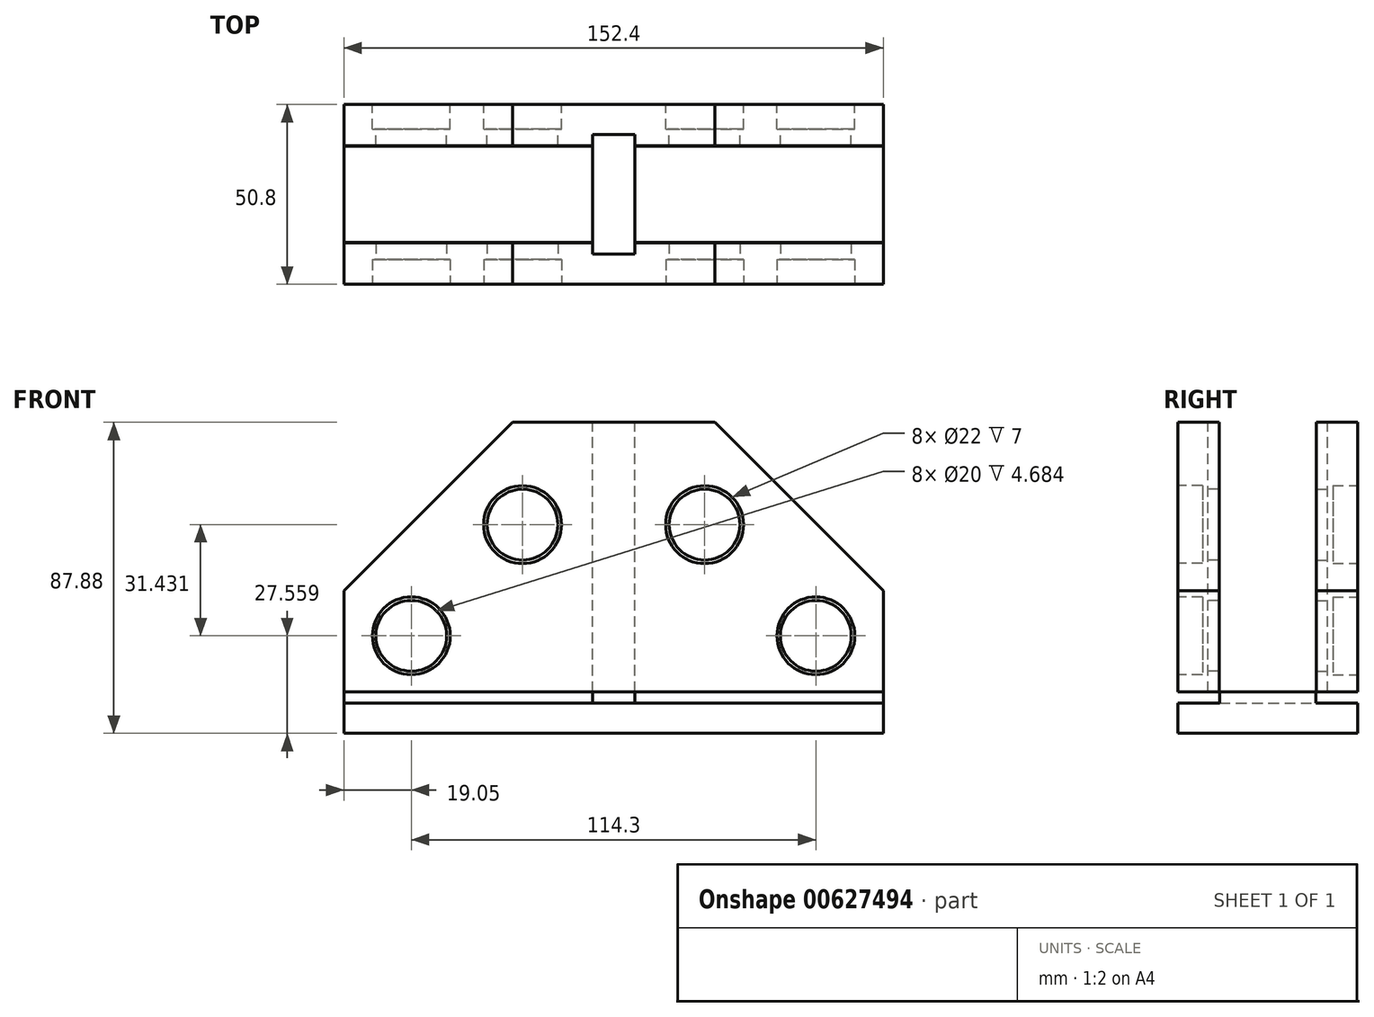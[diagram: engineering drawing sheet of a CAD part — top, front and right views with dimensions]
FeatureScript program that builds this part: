
annotation { "Feature Type Name" : "Feature", "Feature Type Description" : "" }
export const myFeature = defineFeature(function(context is Context, id is Id, definition is map)
    precondition{}
    {
        {
            var Q0;
            Q0=qCreatedBy(makeId("Top.planeOp"),FACE);
            var sketch = newSketch(context, id + "F0", { "sketchPlane" : qUnion([Q0])});
            skLineSegment(sketch, "E0", {"start": v(-76.2, 0) * mm, "end": v(-76.2, 50.8) * mm});
            skLineSegment(sketch, "E1", {"start": v(-76.2, 50.8) * mm, "end": v(76.2, 50.8) * mm});
            skLineSegment(sketch, "E2", {"start": v(76.2, 0) * mm, "end": v(76.2, 50.8) * mm});
            skLineSegment(sketch, "E3", {"start": v(-76.2, 0) * mm, "end": v(76.2, 0) * mm});
            skSolve(sketch);
        }
        {
            var Q0;
            Q0=qSketchRegion(id+"F0",true);
            extrude(context, id + "F1", {"entities" : qUnion([Q0]), "depth" : 11.68 * mm, "offsetDistance" : 25.4 * mm});
        }
        {
            var Q0;
            Q0=makeQuery(id+"F1.opExtrude","SWEPT_FACE",FACE,{"disambiguationData":[OSD([sQuery(id+"F0.wireOp",EDGE,"E1")])]});
            var sketch = newSketch(context, id + "F2", { "sketchPlane" : qUnion([Q0])});
            skLineSegment(sketch, "E4", {"start": v(-76.2, 8.5) * mm, "end": v(76.2, 8.5) * mm});
            skLineSegment(sketch, "E5", {"start": v(76.2, 8.5) * mm, "end": v(76.2, 40.26) * mm});
            skLineSegment(sketch, "E6", {"start": v(76.2, 40.26) * mm, "end": v(28.58, 87.88) * mm});
            skLineSegment(sketch, "E7", {"start": v(28.57, 87.88) * mm, "end": v(-28.57, 87.88) * mm});
            skLineSegment(sketch, "E8", {"start": v(-28.57, 87.88) * mm, "end": v(-76.2, 40.26) * mm});
            skLineSegment(sketch, "E9", {"start": v(-76.2, 40.26) * mm, "end": v(-76.2, 8.5) * mm});
            skSolve(sketch);
        }
        {
            var Q0;
            Q0=qSketchRegion(id+"F2",true);
            extrude(context, id + "F3", {"entities" : qUnion([Q0]), "oppositeDirection" : true, "depth" : 11.68 * mm, "offsetDistance" : 25.4 * mm});
        }
        {
            var Q0;
            Q0=makeQuery(id+"F3.opExtrude","CAP_FACE",FACE,{"disambiguationData":[OSD([sQuery(id+"F2.wireOp",EDGE,"E4"),sQuery(id+"F2.wireOp",EDGE,"E5"),sQuery(id+"F2.wireOp",EDGE,"E6"),sQuery(id+"F2.wireOp",EDGE,"E7"),sQuery(id+"F2.wireOp",EDGE,"E8"),sQuery(id+"F2.wireOp",EDGE,"E9")])],"isStart":true});
            var sketch = newSketch(context, id + "F4", { "sketchPlane" : qUnion([Q0])});
            skCircle(sketch, "E10", {"center": v(-57.15, 27.56) * mm, "radius": 11 * mm});
            skCircle(sketch, "E11", {"center": v(-25.72, 58.99) * mm, "radius": 11 * mm});
            skCircle(sketch, "E12", {"center": v(25.72, 58.99) * mm, "radius": 11 * mm});
            skCircle(sketch, "E13", {"center": v(57.15, 27.56) * mm, "radius": 11 * mm});
            skLineSegment(sketch, "E14", {"start": v(-57.15, 27.56) * mm, "end": v(-25.72, 58.99) * mm, "construction": true});
            skSolve(sketch);
        }
        {
            var Q0;
            Q0=qSketchRegion(id+"F4",true);
            extrude(context, id + "F5", {"entities" : qUnion([Q0]), "operationType" : NewBodyOperationType.REMOVE, "oppositeDirection" : true, "depth" : 7 * mm, "offsetDistance" : 25.4 * mm});
        }
        {
            var Q0;
            Q0=makeQuery(id+"F5.boolean.opBoolean","COPY",FACE,{"derivedFrom":makeQuery(id+"F5.opExtrude","CAP_FACE",FACE,{"disambiguationData":[OSD([sQuery(id+"F4.wireOp",EDGE,"E11")])],"isStart":false})});
            var sketch = newSketch(context, id + "F6", { "sketchPlane" : qUnion([Q0])});
            skCircle(sketch, "E15", {"center": v(-25.72, 58.99) * mm, "radius": 10 * mm});
            skCircle(sketch, "E16", {"center": v(-57.15, 27.56) * mm, "radius": 10 * mm});
            skCircle(sketch, "E17", {"center": v(25.72, 58.99) * mm, "radius": 10 * mm});
            skCircle(sketch, "E18", {"center": v(57.15, 27.56) * mm, "radius": 10 * mm});
            skSolve(sketch);
        }
        {
            var Q0;
            Q0=qSketchRegion(id+"F6",true);
            extrude(context, id + "F7", {"entities" : qUnion([Q0]), "operationType" : NewBodyOperationType.REMOVE, "endBound" : BoundingType.UP_TO_NEXT, "oppositeDirection" : true, "depth" : 25.4 * mm, "offsetDistance" : 25.4 * mm});
        }
        {
            var Q0;
            Q0=makeQuery(id+"F1.opExtrude","CAP_EDGE",EDGE,{"disambiguationData":[OSD([sQuery(id+"F0.wireOp",EDGE,"E0")])],"isStart":false});
            cPoint(context, id + "F8", {"entities" : qUnion([Q0]), "parameter" : 0.5});
        }
        {
            var Q0;
            Q0=makeQuery(id+"F1.opExtrude","CAP_EDGE",EDGE,{"disambiguationData":[OSD([sQuery(id+"F0.wireOp",EDGE,"E0")])],"isStart":true});
            cPoint(context, id + "F9", {"entities" : qUnion([Q0]), "parameter" : 0.5});
        }
        {
            var Q0;
            Q0=makeQuery(id+"F1.opExtrude","CAP_EDGE",EDGE,{"disambiguationData":[OSD([sQuery(id+"F0.wireOp",EDGE,"E2")])],"isStart":false});
            cPoint(context, id + "F10", {"entities" : qUnion([Q0]), "parameter" : 0.5});
        }
        {
            var Q0;
            Q0=qCreatedBy(id+"F8",VERTEX);
            var Q1;
            Q1=qCreatedBy(id+"F9",VERTEX);
            var Q2;
            Q2=qCreatedBy(id+"F10",VERTEX);
            cPlane(context, id + "F11", {"entities" : qUnion([Q0, Q1, Q2]), "cplaneType" : CPlaneType.THREE_POINT, "offset" : 25.4 * mm, "width" : 152.4 * mm, "height" : 152.4 * mm});
        }
        {
            var Q0;
            Q0=makeQuery(id+"F3.opExtrude","SWEPT_BODY",BODY,{"disambiguationData":[OSD([sQuery(id+"F2.wireOp",EDGE,"E4"),sQuery(id+"F2.wireOp",EDGE,"E5"),sQuery(id+"F2.wireOp",EDGE,"E6"),sQuery(id+"F2.wireOp",EDGE,"E7"),sQuery(id+"F2.wireOp",EDGE,"E8"),sQuery(id+"F2.wireOp",EDGE,"E9")])]});
            var Q1;
            Q1=qCreatedBy(id+"F11.planeOp",FACE);
            mirror(context, id + "F12", {"entities" : qUnion([Q0]), "mirrorPlane" : qUnion([Q1])});
        }
        {
            var Q0;
            Q0=makeQuery(id+"F12.opPattern","COPY",FACE,{"derivedFrom":makeQuery(id+"F3.opExtrude","SWEPT_FACE",FACE,{"disambiguationData":[OSD([sQuery(id+"F2.wireOp",EDGE,"E7")])]}),"instanceName":"1"});
            var sketch = newSketch(context, id + "F13", { "sketchPlane" : qUnion([Q0])});
            skLineSegment(sketch, "E19.bottom", {"start": v(-5.84, 42.3) * mm, "end": v(5.84, 42.3) * mm});
            skLineSegment(sketch, "E19.top", {"start": v(-5.84, 8.5) * mm, "end": v(5.84, 8.5) * mm});
            skLineSegment(sketch, "E19.left", {"start": v(-5.84, 42.3) * mm, "end": v(-5.84, 8.5) * mm});
            skLineSegment(sketch, "E19.right", {"start": v(5.84, 42.3) * mm, "end": v(5.84, 8.5) * mm});
            skSolve(sketch);
        }
        {
            var Q0;
            Q0=qSketchRegion(id+"F13",true);
            var Q1;
            Q1=makeQuery(id+"F3.opExtrude","CAP_VERTEX",VERTEX,{"disambiguationData":[OSD([sQuery(id+"F0.wireOp",EDGE,"E1"),sQuery(id+"F0.wireOp",EDGE,"E2"),sQuery(id+"F2.wireOp",EDGE,"E4"),sQuery(id+"F2.wireOp",EDGE,"E9")])],"isStart":true});
            extrude(context, id + "F14", {"entities" : qUnion([Q0]), "endBound" : BoundingType.UP_TO_VERTEX, "oppositeDirection" : true, "depth" : 25.4 * mm, "endBoundEntityVertex" : qUnion([Q1]), "offsetDistance" : 25.4 * mm});
        }
        {
            var Q0;
            Q0=makeQuery(id+"F1.opExtrude","CAP_FACE",FACE,{"disambiguationData":[OSD([sQuery(id+"F0.wireOp",EDGE,"Kr4iFlpK-Gh7r-NuDM-gWga-5seKy08MlqkN"),sQuery(id+"F0.wireOp",EDGE,"hj1FrHpC-pZ17-YCby-A54X-SbDOarESftDo"),sQuery(id+"F0.wireOp",EDGE,"o1bNRVhn-jtSP-6GU1-Arq7-FbX8j65gG8nW"),sQuery(id+"F0.wireOp",EDGE,"E0"),sQuery(id+"F0.wireOp",EDGE,"E1"),sQuery(id+"F0.wireOp",EDGE,"P91Xjv50-tXaL-qIwm-RmlK-IBdr1RYMxtiT"),sQuery(id+"F0.wireOp",EDGE,"E2")])],"isStart":false});
            var sketch = newSketch(context, id + "F15", { "sketchPlane" : qUnion([Q0])});
            skLineSegment(sketch, "E20", {"start": v(-76.2, 50.8) * mm, "end": v(-76.2, 38.99) * mm});
            skLineSegment(sketch, "E21", {"start": v(-76.2, 38.99) * mm, "end": v(-5.97, 38.99) * mm});
            skLineSegment(sketch, "E22", {"start": v(-5.97, 38.99) * mm, "end": v(-5.97, 11.81) * mm});
            skLineSegment(sketch, "E23", {"start": v(-5.97, 11.81) * mm, "end": v(-76.2, 11.81) * mm});
            skLineSegment(sketch, "E24", {"start": v(-76.2, 11.81) * mm, "end": v(-76.2, -0.13) * mm});
            skLineSegment(sketch, "E25", {"start": v(-76.2, -0.13) * mm, "end": v(76.2, -0.13) * mm});
            skLineSegment(sketch, "E26", {"start": v(76.2, -0.13) * mm, "end": v(76.2, 11.81) * mm});
            skLineSegment(sketch, "E27", {"start": v(76.2, 11.81) * mm, "end": v(5.97, 11.81) * mm});
            skLineSegment(sketch, "E28", {"start": v(5.97, 11.81) * mm, "end": v(5.97, 38.99) * mm});
            skLineSegment(sketch, "E29", {"start": v(5.97, 38.99) * mm, "end": v(76.2, 38.99) * mm});
            skLineSegment(sketch, "E30", {"start": v(76.2, 38.99) * mm, "end": v(76.2, 50.8) * mm});
            skLineSegment(sketch, "E31", {"start": v(76.2, 50.8) * mm, "end": v(-76.2, 50.8) * mm});
            skSolve(sketch);
        }
        {
            var Q0;
            Q0=qSketchRegion(id+"F15",true);
            var Q1;
            Q1=makeQuery(id+"F12.opPattern","COPY",VERTEX,{"derivedFrom":makeQuery(id+"F3.opExtrude","CAP_VERTEX",VERTEX,{"disambiguationData":[OSD([sQuery(id+"F0.wireOp",EDGE,"E0"),sQuery(id+"F0.wireOp",EDGE,"E1"),sQuery(id+"F2.wireOp",EDGE,"E4"),sQuery(id+"F2.wireOp",EDGE,"E5")])],"isStart":false}),"instanceName":"1"});
            extrude(context, id + "F16", {"entities" : qUnion([Q0]), "operationType" : NewBodyOperationType.REMOVE, "endBound" : BoundingType.UP_TO_VERTEX, "oppositeDirection" : true, "depth" : 25.4 * mm, "endBoundEntityVertex" : qUnion([Q1]), "offsetDistance" : 25.4 * mm});
        }
        {
            var Q0;
            Q0=makeQuery(id+"F3.opExtrude","SWEPT_FACE",FACE,{"disambiguationData":[OSD([sQuery(id+"F2.wireOp",EDGE,"E7")])]});
            var sketch = newSketch(context, id + "F17", { "sketchPlane" : qUnion([Q0])});
            skLineSegment(sketch, "E32.bottom", {"start": v(-5.97, 42.3) * mm, "end": v(5.97, 42.3) * mm});
            skLineSegment(sketch, "E32.top", {"start": v(-5.97, 8.5) * mm, "end": v(5.97, 8.5) * mm});
            skLineSegment(sketch, "E32.left", {"start": v(-5.97, 42.3) * mm, "end": v(-5.97, 8.5) * mm});
            skLineSegment(sketch, "E32.right", {"start": v(5.97, 42.3) * mm, "end": v(5.97, 8.5) * mm});
            skSolve(sketch);
        }
        {
            var Q0;
            Q0=qSketchRegion(id+"F17",true);
            var Q1;
            Q1=makeQuery(id+"F16.boolean.opBoolean","COPY",VERTEX,{"derivedFrom":makeQuery(id+"F16.opExtrude","CAP_VERTEX",VERTEX,{"disambiguationData":[OSD([sQuery(id+"F15.wireOp",EDGE,"E20"),sQuery(id+"F15.wireOp",EDGE,"E31"),dummyQuery(id+"F16.vertexPlane.planeOp",FACE)])],"isStart":false})});
            extrude(context, id + "F18", {"entities" : qUnion([Q0]), "operationType" : NewBodyOperationType.REMOVE, "endBound" : BoundingType.UP_TO_VERTEX, "oppositeDirection" : true, "depth" : 25.4 * mm, "endBoundEntityVertex" : qUnion([Q1]), "offsetDistance" : 25.4 * mm});
        }
    });
